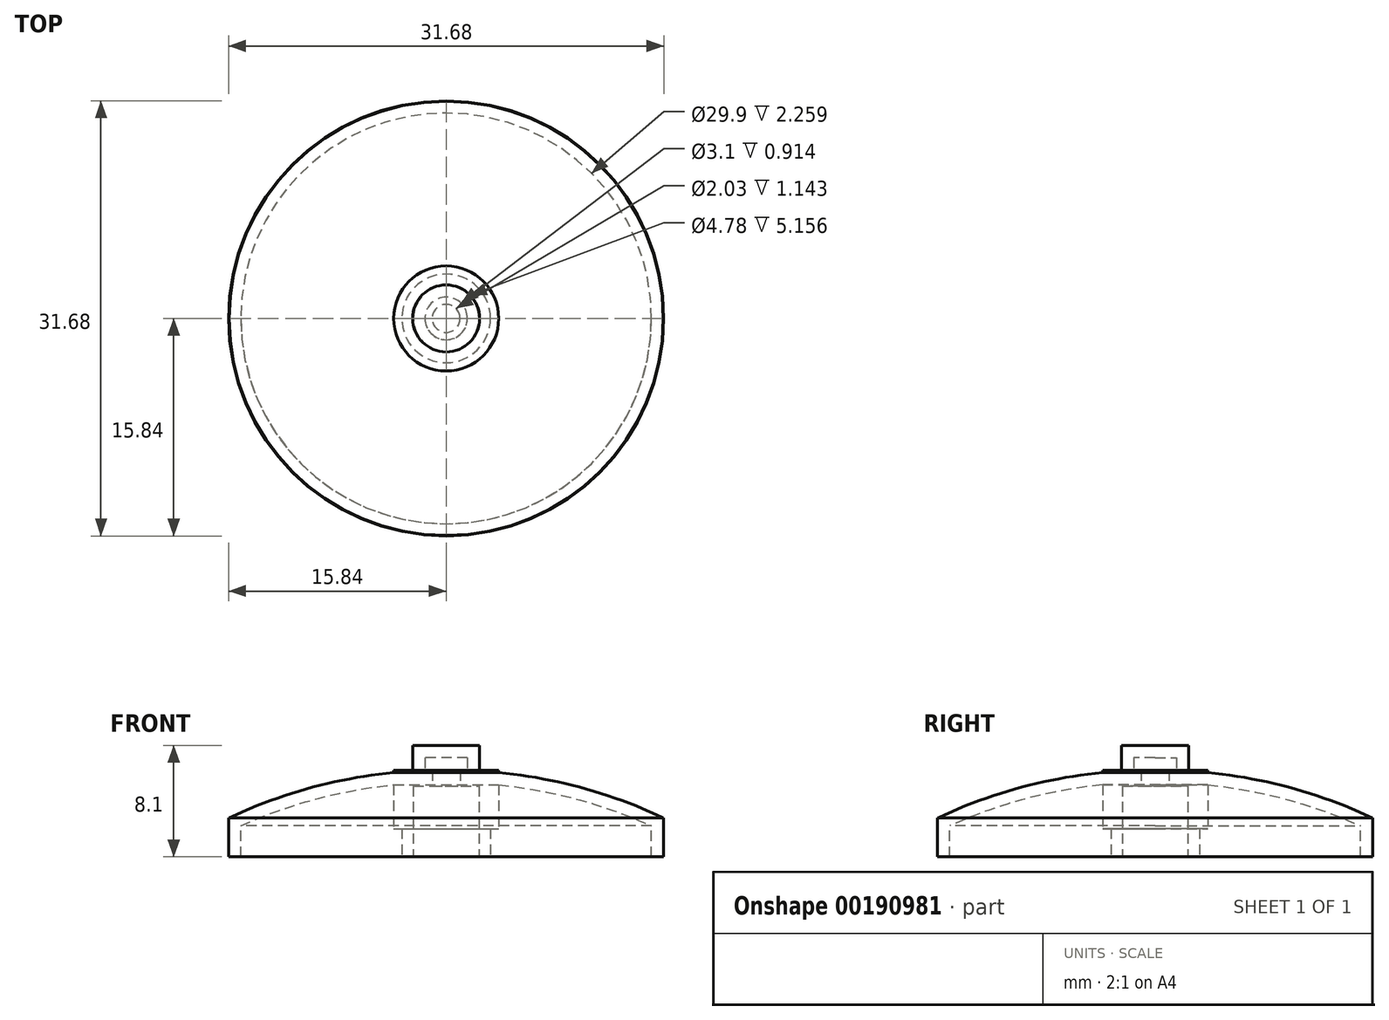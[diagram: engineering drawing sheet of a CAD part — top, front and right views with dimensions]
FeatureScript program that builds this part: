
annotation { "Feature Type Name" : "Feature", "Feature Type Description" : "" }
export const myFeature = defineFeature(function(context is Context, id is Id, definition is map)
    precondition{}
    {
        {
            var Q0;
            Q0=qCreatedBy(makeId("Top.planeOp"),FACE);
            var sketch = newSketch(context, id + "F0", { "sketchPlane" : qUnion([Q0])});
            skCircle(sketch, "E0", {"center": v(0, 0) * mm, "radius": 15.84 * mm});
            skSolve(sketch);
        }
        {
            var Q0;
            Q0 = qSketchRegion(id + "F0", true);
            extrude(context, id + "F1", {"entities" : qUnion([Q0]), "oppositeDirection" : true, "depth" : 2.84 * mm});
        }
        {
            var Q0;
            Q0=qCreatedBy(makeId("Front.planeOp"),FACE);
            var sketch = newSketch(context, id + "F2", { "sketchPlane" : qUnion([Q0])});
            skLineSegment(sketch, "E1", {"start": v(0, 0) * mm, "end": v(0, 3.45) * mm, "construction": true});
            skArc(sketch, "E2", {"start": v(15.12, 0) * mm, "mid": v(-0.34, 3.46) * mm, "end": v(-15.8, 0) * mm});
            skLineSegment(sketch, "E3", {"start": v(0, 3.45) * mm, "end": v(0, 0) * mm});
            skLineSegment(sketch, "E4", {"start": v(-15.8, 0) * mm, "end": v(15.12, 0) * mm});
            skSolve(sketch);
        }
        {
            var Q0;
            Q0=qCreatedBy(makeId("Front.planeOp"),FACE);
            var sketch = newSketch(context, id + "F3", { "sketchPlane" : qUnion([Q0])});
            skLineSegment(sketch, "E5", {"start": v(0, 18.5) * mm, "end": v(0, -30.43) * mm});
            skSolve(sketch);
        }
        {
            var Q0;
            {var subQ3=sQuery(id+"F2.wireOp",EDGE,"E3");Q0=makeQuery(id+"F2.imprint","IMPRINT",FACE,{"disambiguationData":[TD([[makeQuery(id+"F2.imprint","IMPRINT",EDGE,{"derivedFrom":subQ3}),-1.0]])]});}
            var Q1;
            Q1=sQuery(id+"F3.wireOp",EDGE,"E5");
            revolve(context, id + "F4", {"operationType" : NewBodyOperationType.ADD, "entities" : qUnion([Q0]), "axis" : qUnion([Q1]), "revolveType" : RevolveType.FULL});
        }
        {
            var Q0;
            Q0=qCreatedBy(makeId("Top.planeOp"),FACE);
            cPlane(context, id + "F5", {"entities" : qUnion([Q0]), "cplaneType" : CPlaneType.OFFSET, "offset" : 3.45 * mm, "width" : 152.4 * mm, "height" : 152.4 * mm});
        }
        {
            var Q0;
            Q0=qCreatedBy(id+"F5.planeOp",FACE);
            var sketch = newSketch(context, id + "F6", { "sketchPlane" : qUnion([Q0])});
            skCircle(sketch, "E6", {"center": v(0, 0) * mm, "radius": 2.44 * mm});
            skSolve(sketch);
        }
        {
            var Q0;
            Q0 = qSketchRegion(id + "F6", true);
            var Q1;
            Q1=sQuery(id+"F6.wireOp",EDGE,"E6");
            extrude(context, id + "F7", {"entities" : qUnion([Q0]), "surfaceEntities" : qUnion([Q1]), "depth" : 1.8 * mm});
        }
        {
            var Q0;
            Q0=qCreatedBy(id+"F5.planeOp",FACE);
            var sketch = newSketch(context, id + "F8", { "sketchPlane" : qUnion([Q0])});
            skCircle(sketch, "E7", {"center": v(0, 0) * mm, "radius": 3.66 * mm});
            skSolve(sketch);
        }
        {
            var Q0;
            Q0 = qSketchRegion(id + "F8", true);
            extrude(context, id + "F9", {"entities" : qUnion([Q0]), "operationType" : NewBodyOperationType.ADD, "oppositeDirection" : true, "depth" : 5.08 * mm});
        }
        {
            var Q0;
            Q0=makeQuery(id+"F1.opExtrude","CAP_FACE",FACE,{"disambiguationData":[OSD([sQuery(id+"F0.wireOp",EDGE,"E0")])],"isStart":false});
            shell(context, id + "F10", {"entities" : qUnion([Q0]), "thickness" : 0.89 * mm});
        }
        {
            var Q0;
            Q0=makeQuery(id+"F1.opExtrude","CAP_FACE",FACE,{"disambiguationData":[OSD([sQuery(id+"F0.wireOp",EDGE,"E0")])],"isStart":false});
            cPlane(context, id + "F11", {"entities" : qUnion([Q0]), "cplaneType" : CPlaneType.OFFSET, "offset" : 0 * mm, "width" : 152.4 * mm, "height" : 152.4 * mm});
        }
        {
            var Q0;
            Q0=qCreatedBy(id+"F11.planeOp",FACE);
            var sketch = newSketch(context, id + "F12", { "sketchPlane" : qUnion([Q0])});
            skCircle(sketch, "E8", {"center": v(0, 0) * mm, "radius": 3.82 * mm});
            skSolve(sketch);
        }
        {
            var Q0;
            Q0 = qSketchRegion(id + "F12", true);
            extrude(context, id + "F13", {"entities" : qUnion([Q0]), "operationType" : NewBodyOperationType.ADD, "oppositeDirection" : true, "depth" : 6.3 * mm});
        }
        {
            var Q0;
            Q0=makeQuery(id+"F13.opExtrude","CAP_FACE",FACE,{"disambiguationData":[OSD([sQuery(id+"F12.wireOp",EDGE,"E8")])],"isStart":true});
            var sketch = newSketch(context, id + "F14", { "sketchPlane" : qUnion([Q0])});
            skCircle(sketch, "E9", {"center": v(0, 0) * mm, "radius": 1.02 * mm});
            skSolve(sketch);
        }
        {
            var Q0;
            Q0 = qSketchRegion(id + "F14", true);
            extrude(context, id + "F15", {"entities" : qUnion([Q0]), "operationType" : NewBodyOperationType.REMOVE, "oppositeDirection" : true, "depth" : 6.86 * mm});
        }
        {
            var Q0;
            Q0=makeQuery(id+"F13.opExtrude","CAP_FACE",FACE,{"disambiguationData":[OSD([sQuery(id+"F12.wireOp",EDGE,"E8")])],"isStart":true});
            var sketch = newSketch(context, id + "F16", { "sketchPlane" : qUnion([Q0])});
            skCircle(sketch, "E10", {"center": v(0, 0) * mm, "radius": 2.39 * mm});
            skSolve(sketch);
        }
        {
            var Q0;
            Q0 = qSketchRegion(id + "F16", true);
            extrude(context, id + "F17", {"entities" : qUnion([Q0]), "operationType" : NewBodyOperationType.REMOVE, "oppositeDirection" : true, "depth" : 5.16 * mm});
        }
        {
            var Q0;
            Q0=qCreatedBy(id+"F11.planeOp",FACE);
            var sketch = newSketch(context, id + "F18", { "sketchPlane" : qUnion([Q0])});
            skCircle(sketch, "E11", {"center": v(0, 0) * mm, "radius": 3.82 * mm});
            skSolve(sketch);
        }
        {
            var Q0;
            Q0 = qSketchRegion(id + "F18", true);
            extrude(context, id + "F19", {"entities" : qUnion([Q0]), "operationType" : NewBodyOperationType.REMOVE, "oppositeDirection" : true, "depth" : 2.06 * mm});
        }
        {
            var Q0;
            Q0=qCreatedBy(id+"F11.planeOp",FACE);
            var sketch = newSketch(context, id + "F20", { "sketchPlane" : qUnion([Q0])});
            skCircle(sketch, "E12", {"center": v(0, 0) * mm, "radius": 3.23 * mm});
            skCircle(sketch, "E13", {"center": v(0, 0) * mm, "radius": 2.39 * mm});
            skSolve(sketch);
        }
        {
            var Q0;
            Q0 = qSketchRegion(id + "F20", true);
            extrude(context, id + "F21", {"entities" : qUnion([Q0]), "operationType" : NewBodyOperationType.ADD, "oppositeDirection" : true, "depth" : 2.06 * mm});
        }
    });
